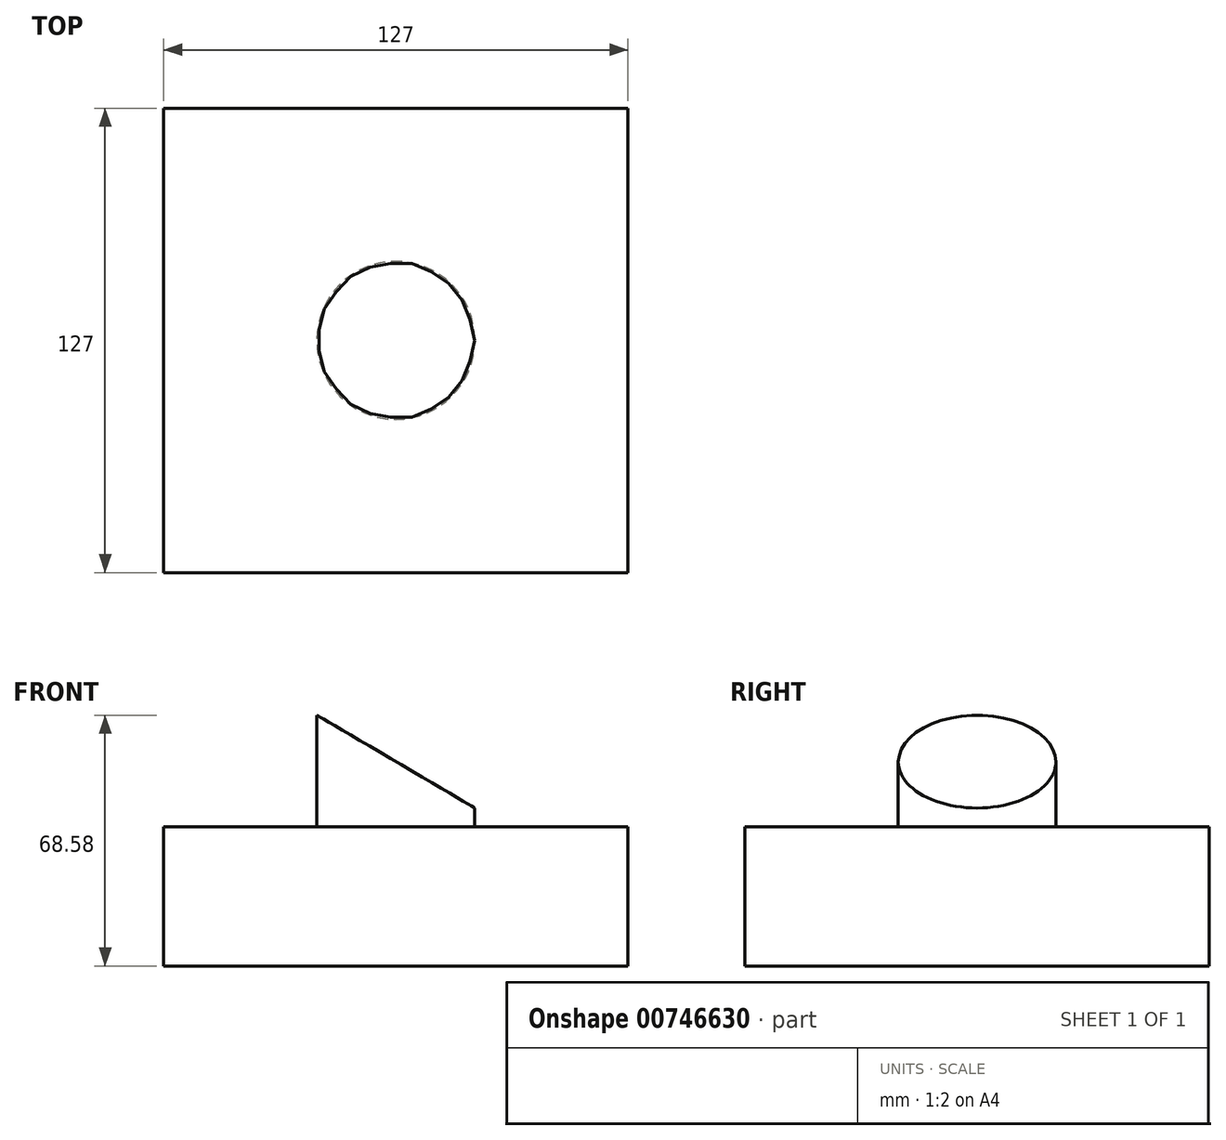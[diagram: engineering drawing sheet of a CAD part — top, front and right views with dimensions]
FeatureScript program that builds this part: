
annotation { "Feature Type Name" : "Feature", "Feature Type Description" : "" }
export const myFeature = defineFeature(function(context is Context, id is Id, definition is map)
    precondition{}
    {
        {
            var Q0;
            Q0=qCreatedBy(makeId("Top.planeOp"),FACE);
            var sketch = newSketch(context, id + "F0", { "sketchPlane" : qUnion([Q0])});
            skLineSegment(sketch, "E0.bottom", {"start": v(-63.5, 63.5) * mm, "end": v(63.5, 63.5) * mm});
            skLineSegment(sketch, "E0.top", {"start": v(-63.5, -63.5) * mm, "end": v(63.5, -63.5) * mm});
            skLineSegment(sketch, "E0.left", {"start": v(-63.5, 63.5) * mm, "end": v(-63.5, -63.5) * mm});
            skLineSegment(sketch, "E0.right", {"start": v(63.5, 63.5) * mm, "end": v(63.5, -63.5) * mm});
            skSolve(sketch);
        }
        {
            var Q0;
            Q0=makeQuery(id+"F0.imprint","IMPRINT",FACE,{"disambiguationData":[TD([[makeQuery(id+"F0.imprint","IMPRINT",EDGE,{"derivedFrom":sQuery(id+"F0.wireOp",EDGE,"E0.bottom")}),-1.0]])]});
            extrude(context, id + "F1", {"entities" : qUnion([Q0]), "depth" : 38.1 * mm, "offsetDistance" : 25.4 * mm});
        }
        {
            var Q0;
            Q0=makeQuery(id+"F1.opExtrude","CAP_FACE",FACE,{"disambiguationData":[OSD([sQuery(id+"F0.wireOp",EDGE,"E0.bottom"),sQuery(id+"F0.wireOp",EDGE,"E0.top"),sQuery(id+"F0.wireOp",EDGE,"E0.left"),sQuery(id+"F0.wireOp",EDGE,"E0.right")])],"isStart":false});
            var sketch = newSketch(context, id + "F2", { "sketchPlane" : qUnion([Q0])});
            skCircle(sketch, "E1", {"center": v(0, 0) * mm, "radius": 21.59 * mm});
            skSolve(sketch);
        }
        {
            var Q0;
            Q0=makeQuery(id+"F2.imprint","IMPRINT",FACE,{"disambiguationData":[TD([[makeQuery(id+"F2.imprint","IMPRINT",EDGE,{"derivedFrom":sQuery(id+"F2.wireOp",EDGE,"E1")}),-1.0]])]});
            cPlane(context, id + "F3", {"entities" : qUnion([Q0]), "cplaneType" : CPlaneType.OFFSET, "offset" : 25.4 * mm, "width" : 152.4 * mm, "height" : 152.4 * mm});
        }
        {
            var Q0;
            Q0=makeQuery(id+"F2.imprint","IMPRINT",FACE,{"disambiguationData":[TD([[makeQuery(id+"F2.imprint","IMPRINT",EDGE,{"derivedFrom":sQuery(id+"F2.wireOp",EDGE,"E1")}),1.0]])]});
            extrude(context, id + "F4", {"entities" : qUnion([Q0]), "operationType" : NewBodyOperationType.ADD, "depth" : 30.48 * mm, "offsetDistance" : 25.4 * mm});
        }
        {
            var Q0;
            Q0=qCreatedBy(makeId("Front.planeOp"),FACE);
            cPlane(context, id + "F5", {"entities" : qUnion([Q0]), "cplaneType" : CPlaneType.OFFSET, "offset" : 25.4 * mm, "width" : 152.4 * mm, "height" : 152.4 * mm});
        }
        {
            var Q0;
            Q0=qCreatedBy(id+"F5.planeOp",FACE);
            var sketch = newSketch(context, id + "F6", { "sketchPlane" : qUnion([Q0])});
            skLineSegment(sketch, "E2", {"start": v(-21.6, 68.58) * mm, "end": v(21.6, 68.58) * mm});
            skLineSegment(sketch, "E3", {"start": v(21.6, 68.58) * mm, "end": v(21.6, 43.18) * mm});
            skLineSegment(sketch, "E4", {"start": v(21.6, 43.18) * mm, "end": v(-21.6, 68.58) * mm});
            skSolve(sketch);
        }
        {
            var Q0;
            Q0=makeQuery(id+"F6.imprint","IMPRINT",FACE,{"disambiguationData":[TD([[makeQuery(id+"F6.imprint","IMPRINT",EDGE,{"derivedFrom":sQuery(id+"F6.wireOp",EDGE,"E2")}),-1.0]])]});
            extrude(context, id + "F7", {"entities" : qUnion([Q0]), "operationType" : NewBodyOperationType.REMOVE, "oppositeDirection" : true, "depth" : 1270 * mm, "offsetDistance" : 25.4 * mm});
        }
    });
